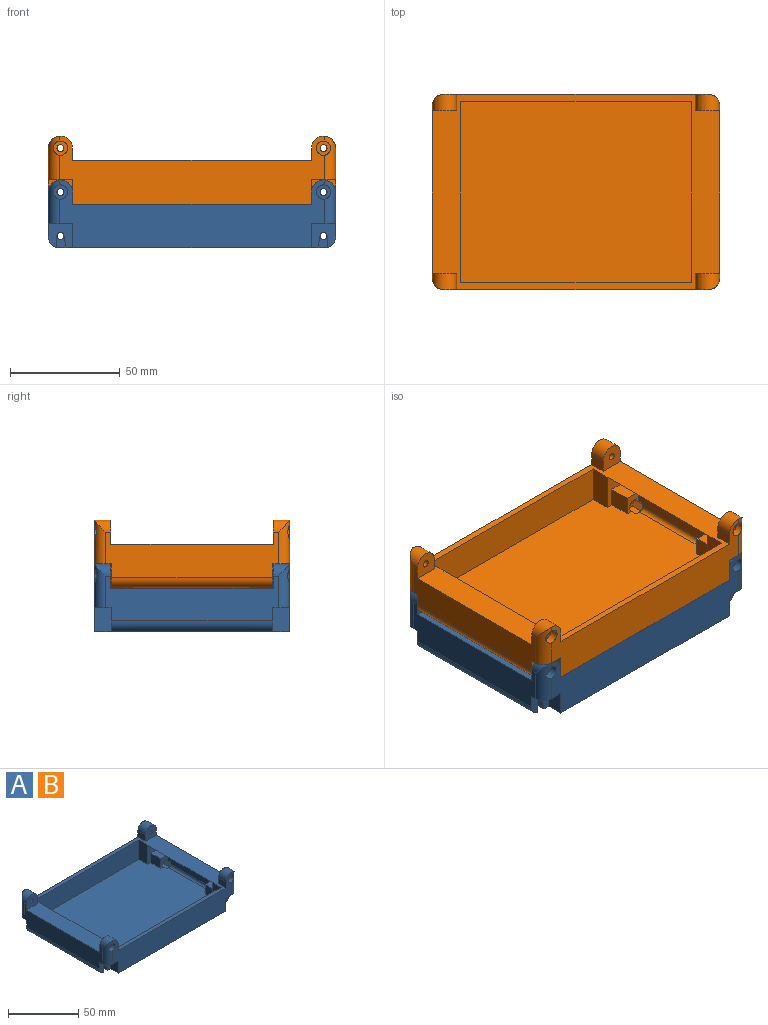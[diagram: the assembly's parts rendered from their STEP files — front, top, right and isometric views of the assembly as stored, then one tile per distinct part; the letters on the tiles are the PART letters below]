
ASSEMBLY  parts=2 mates=1
PART A: 125 faces, bbox 131x89x31 mm
  f0: cylinder r=1.6mm len=11.3mm, axis (0,-1,0), area 60.7mm2, adj f2,f120,f122,f123,f124
  f1: cylinder r=5mm len=73.6mm, axis (0,1,0), area 555.9mm2, adj f2,f8,f32,f33,f108,f110,f122,f124
  f2: plane 11.2x11mm, normal (0,-1,0), area 93.6mm2, adj f0,f1,f32,f33,f45,f46,f122,f123
  f3: plane 121x83mm, normal (0,0,1), area 9527.3mm2, adj f5,f19,f28,f29,f30,f31,f34,f35
  f4: plane 45x6.54mm, normal (-1,0,0), area 283.4mm2, adj f5,f34,f60,f64,f100,f107,f114,f121
  f5: plane 8.54x7mm, normal (0,1,0), area 34mm2, adj f3,f4,f58,f59,f114,f117,f118,f119
  f6: plane 121x31mm, normal (0,-1,0), area 2363mm2, adj f7,f14,f25,f26,f33,f40,f45,f46
  f7: cylinder r=5mm len=19.98mm, axis (0,0,-1), area 126.6mm2, adj f6,f32,f46,f65,f113
  f8: plane 11.2x11mm, normal (0,1,0), area 93.6mm2, adj f1,f9,f32,f33,f47,f48,f108,f109
  f9: cylinder r=1.6mm len=11.3mm, axis (0,1,0), area 60.7mm2, adj f8,f106,f108,f109,f110
  f10: plane 121x31mm, normal (0,1,0), area 2363mm2, adj f11,f20,f33,f36,f39,f40,f47,f48
  f11: cylinder r=5mm len=19.98mm, axis (0,0,-1), area 126.6mm2, adj f10,f32,f48,f68,f99
  f12: plane 11.2x11mm, normal (0,-1,0), area 93.6mm2, adj f13,f16,f27,f33,f49,f50,f94,f95
  f13: cylinder r=1.6mm len=11.3mm, axis (0,-1,0), area 60.7mm2, adj f12,f93,f94,f95,f96
  f14: cylinder r=5mm len=19.98mm, axis (0,0,-1), area 126.6mm2, adj f6,f27,f50,f67,f85
  f15: cylinder r=1.6mm len=11.3mm, axis (0,1,0), area 60.7mm2, adj f17,f79,f80,f81,f82
  f16: cylinder r=5mm len=73.6mm, axis (0,-1,0), area 555.9mm2, adj f12,f17,f27,f33,f80,f82,f94,f96
  f17: plane 11.2x11mm, normal (0,1,0), area 93.6mm2, adj f15,f16,f27,f33,f51,f52,f80,f81
  f18: plane 45x6.54mm, normal (1,0,0), area 283.4mm2, adj f19,f38,f53,f63,f72,f73,f86,f87
  f19: plane 8.54x7mm, normal (0,-1,0), area 34mm2, adj f3,f18,f56,f57,f73,f76,f77,f78
  f20: cylinder r=5mm len=19.98mm, axis (0,0,-1), area 126.6mm2, adj f10,f27,f52,f66,f71
  f21: plane 11x11mm, normal (0,1,0), area 100mm2, adj f25,f32,f40,f65,f111
  f22: plane 11x11mm, normal (0,-1,0), area 100mm2, adj f32,f36,f40,f68,f97
  f23: plane 11x11mm, normal (0,1,0), area 100mm2, adj f26,f27,f40,f67,f83
  f24: plane 11x11mm, normal (0,-1,0), area 100mm2, adj f27,f39,f40,f66,f69
  f25: plane 7.5x5.5mm, normal (-1,0,0), area 41.2mm2, adj f6,f21,f40,f65
  f26: plane 7.5x5.5mm, normal (1,0,0), area 41.2mm2, adj f6,f23,f40,f67
  f27: plane 79x20.5mm, normal (-1,0,0), area 1180.1mm2, adj f12,f14,f16,f17,f20,f23,f24,f40
  f28: plane 17x10mm, normal (0,1,0), area 67.9mm2, adj f3,f44,f58,f59,f64
  f29: plane 17x10mm, normal (0,1,0), area 67.9mm2, adj f3,f42,f54,f55,f63
  f30: plane 17x10mm, normal (0,-1,0), area 67.9mm2, adj f3,f43,f61,f62,f64
  f31: plane 17x10mm, normal (0,-1,0), area 67.9mm2, adj f3,f41,f56,f57,f63
  f32: plane 79x20.5mm, normal (1,0,0), area 1180.1mm2, adj f1,f2,f7,f8,f11,f21,f22,f40
  f33: plane 121x89mm, normal (0,0,-1), area 10456.2mm2, adj f1,f2,f6,f8,f10,f12,f16,f17
  f34: cylinder r=2mm len=39mm, axis (0,1,0), area 122.5mm2, adj f3,f4,f107,f121
  f35: plane 105x17mm, normal (0,1,0), area 1785mm2, adj f3,f40,f42,f44
  f36: plane 7.5x5.5mm, normal (-1,0,0), area 41.2mm2, adj f10,f22,f40,f68
  f37: plane 105x17mm, normal (0,-1,0), area 1785mm2, adj f3,f40,f41,f43
  f38: cylinder r=2mm len=39mm, axis (0,-1,0), area 122.5mm2, adj f3,f18,f72,f86
  f39: plane 7.5x5.5mm, normal (1,0,0), area 41.2mm2, adj f10,f24,f40,f66
  f40: plane 131x89mm, normal (0,0,1), area 2614mm2, adj f6,f10,f21,f22,f23,f24,f25,f26
  f41: plane 17x9mm, normal (1,0,0), area 153mm2, adj f3,f31,f37,f40
  f42: plane 17x9mm, normal (1,0,0), area 153mm2, adj f3,f29,f35,f40
  f43: plane 17x9mm, normal (-1,0,0), area 153mm2, adj f3,f30,f37,f40
  f44: plane 17x9mm, normal (-1,0,0), area 153mm2, adj f3,f28,f35,f40
  f45: plane 11x7.7mm, normal (1,0,0), area 84.7mm2, adj f2,f6,f33,f46
  f46: plane 11.2x7.7mm, normal (0,0,-1), area 80.9mm2, adj f2,f6,f7,f32,f45
  f47: plane 11x7.7mm, normal (1,0,0), area 84.7mm2, adj f8,f10,f33,f48
  f48: plane 11.2x7.7mm, normal (0,0,-1), area 80.9mm2, adj f8,f10,f11,f32,f47
  f49: plane 11x7.7mm, normal (-1,0,0), area 84.7mm2, adj f6,f12,f33,f50
  f50: plane 11.2x7.7mm, normal (0,0,-1), area 80.9mm2, adj f6,f12,f14,f27,f49
  f51: plane 11x7.7mm, normal (-1,0,0), area 84.7mm2, adj f10,f17,f33,f52
  f52: plane 11.2x7.7mm, normal (0,0,-1), area 80.9mm2, adj f10,f17,f20,f27,f51
  f53: plane 8.54x7mm, normal (0,1,0), area 34mm2, adj f3,f18,f54,f55,f87,f88,f89,f90
  f54: plane 10x7mm, normal (0,0,1), area 70mm2, adj f29,f53,f55,f63
  f55: plane 10x8.54mm, normal (1,0,0), area 85.4mm2, adj f3,f29,f53,f54
  f56: plane 10x8.54mm, normal (1,0,0), area 85.4mm2, adj f3,f19,f31,f57
  f57: plane 10x7mm, normal (0,0,1), area 70mm2, adj f19,f31,f56,f63
  f58: plane 10x8.54mm, normal (-1,0,0), area 85.4mm2, adj f3,f5,f28,f59
  f59: plane 10x7mm, normal (0,0,1), area 70mm2, adj f5,f28,f58,f64
  f60: plane 8.54x7mm, normal (0,-1,0), area 34mm2, adj f3,f4,f61,f62,f100,f101,f102,f103
  f61: plane 10x7mm, normal (0,0,1), area 70mm2, adj f30,f60,f62,f64
  f62: plane 10x8.54mm, normal (-1,0,0), area 85.4mm2, adj f3,f30,f60,f61
  f63: plane 65x10mm, normal (0.65,0,-0.76), area 851.5mm2, adj f18,f29,f31,f40,f54,f57
  f64: plane 65x10mm, normal (-0.65,0,-0.76), area 851.5mm2, adj f4,f28,f30,f40,f59,f61
  f65: cylinder r=5.5mm len=11mm, axis (0,1,0), area 114.7mm2, adj f6,f7,f21,f25,f32
  f66: cylinder r=5.5mm len=11mm, axis (0,1,0), area 114.7mm2, adj f10,f20,f24,f27,f39
  f67: cylinder r=5.5mm len=11mm, axis (0,1,0), area 114.7mm2, adj f6,f14,f23,f26,f27
  f68: cylinder r=5.5mm len=11mm, axis (0,1,0), area 114.7mm2, adj f10,f11,f22,f32,f36
  f69: cylinder r=1.6mm len=3.68mm, axis (0,1,0), area 37mm2, adj f24,f70
  f70: plane 6.5x6.5mm, normal (0,1,0), area 25.1mm2, adj f69,f71
  f71: cylinder r=3.25mm len=6.5mm, axis (0,1,0), area 74.3mm2, adj f10,f20,f70
  f72: plane 5.06x4.11mm, normal (0,1,0), area 2.5mm2, adj f3,f18,f38,f73,f74,f75,f76
  f73: plane 6x2.81mm, normal (0.87,0,-0.5), area 14.3mm2, adj f18,f19,f72,f74,f78,f79
  f74: plane 6x2.81mm, normal (0.87,0,0.5), area 19.5mm2, adj f72,f73,f75,f79
  f75: plane 6x3.25mm, normal (0,0,1), area 19.5mm2, adj f72,f74,f76,f79
  f76: plane 6x2.81mm, normal (-0.87,0,0.5), area 10.8mm2, adj f3,f19,f72,f75,f77,f79
  f77: plane 3x2.81mm, normal (-0.87,0,-0.5), area 9.8mm2, adj f19,f76,f78,f79
  f78: plane 3.25x3mm, normal (0,0,-1), area 9.7mm2, adj f19,f73,f77,f79
  f79: plane 6.5x5.63mm, normal (0,-1,0), area 19.4mm2, adj f15,f73,f74,f75,f76,f77,f78
  f80: plane 10x5.38mm, normal (1,0,0), area 53.8mm2, adj f15,f16,f17,f82
  f81: plane 10x5.77mm, normal (-0.99,0,-0.17), area 58.5mm2, adj f15,f17,f33,f82
  f82: plane 5.76x4.15mm, normal (0,1,0), area 16.2mm2, adj f15,f16,f33,f80,f81
  f83: cylinder r=1.6mm len=3.68mm, axis (0,-1,0), area 37mm2, adj f23,f84
  f84: plane 6.5x6.5mm, normal (0,-1,0), area 25.1mm2, adj f83,f85
  f85: cylinder r=3.25mm len=6.5mm, axis (0,-1,0), area 74.3mm2, adj f6,f14,f84
  f86: plane 5.06x4.11mm, normal (0,-1,0), area 2.5mm2, adj f3,f18,f38,f87,f90,f91,f92
  f87: plane 6x2.81mm, normal (0.87,0,-0.5), area 14.3mm2, adj f18,f53,f86,f88,f92,f93
  f88: plane 3.25x3mm, normal (0,0,-1), area 9.7mm2, adj f53,f87,f89,f93
  f89: plane 3x2.81mm, normal (-0.87,0,-0.5), area 9.8mm2, adj f53,f88,f90,f93
  f90: plane 6x2.81mm, normal (-0.87,0,0.5), area 10.8mm2, adj f3,f53,f86,f89,f91,f93
  f91: plane 6x3.25mm, normal (0,0,1), area 19.5mm2, adj f86,f90,f92,f93
  f92: plane 6x2.81mm, normal (0.87,0,0.5), area 19.5mm2, adj f86,f87,f91,f93
  f93: plane 6.5x5.63mm, normal (0,1,0), area 19.4mm2, adj f13,f87,f88,f89,f90,f91,f92
  f94: plane 10x5.38mm, normal (1,0,0), area 53.8mm2, adj f12,f13,f16,f96
  f95: plane 10x5.77mm, normal (-0.99,0,-0.17), area 58.5mm2, adj f12,f13,f33,f96
  f96: plane 5.76x4.15mm, normal (0,-1,0), area 16.2mm2, adj f13,f16,f33,f94,f95
  f97: cylinder r=1.6mm len=3.68mm, axis (0,1,0), area 37mm2, adj f22,f98
  f98: plane 6.5x6.5mm, normal (0,1,0), area 25.1mm2, adj f97,f99
  f99: cylinder r=3.25mm len=6.5mm, axis (0,1,0), area 74.3mm2, adj f10,f11,f98
  f100: plane 6x2.81mm, normal (-0.87,0,-0.5), area 14.3mm2, adj f4,f60,f101,f105,f106,f107
  f101: plane 3.25x3mm, normal (0,0,-1), area 9.7mm2, adj f60,f100,f102,f106
  f102: plane 3x2.81mm, normal (0.87,0,-0.5), area 9.8mm2, adj f60,f101,f103,f106
  f103: plane 6x2.81mm, normal (0.87,0,0.5), area 10.8mm2, adj f3,f60,f102,f104,f106,f107
  f104: plane 6x3.25mm, normal (0,0,1), area 19.5mm2, adj f103,f105,f106,f107
  f105: plane 6x2.81mm, normal (-0.87,0,0.5), area 19.5mm2, adj f100,f104,f106,f107
  f106: plane 6.5x5.63mm, normal (0,-1,0), area 19.4mm2, adj f9,f100,f101,f102,f103,f104,f105
  f107: plane 5.06x4.11mm, normal (0,1,0), area 2.5mm2, adj f3,f4,f34,f100,f103,f104,f105
  f108: plane 10x5.38mm, normal (-1,0,0), area 53.8mm2, adj f1,f8,f9,f110
  f109: plane 10x5.77mm, normal (0.99,0,-0.17), area 58.5mm2, adj f8,f9,f33,f110
  f110: plane 5.76x4.15mm, normal (0,1,0), area 16.2mm2, adj f1,f9,f33,f108,f109
  f111: cylinder r=1.6mm len=3.68mm, axis (0,-1,0), area 37mm2, adj f21,f112
  f112: plane 6.5x6.5mm, normal (0,-1,0), area 25.1mm2, adj f111,f113
  f113: cylinder r=3.25mm len=6.5mm, axis (0,-1,0), area 74.3mm2, adj f6,f7,f112
  f114: plane 6x2.81mm, normal (-0.87,0,-0.5), area 14.3mm2, adj f4,f5,f115,f119,f120,f121
  f115: plane 6x2.81mm, normal (-0.87,0,0.5), area 19.5mm2, adj f114,f116,f120,f121
  f116: plane 6x3.25mm, normal (0,0,1), area 19.5mm2, adj f115,f117,f120,f121
  f117: plane 6x2.81mm, normal (0.87,0,0.5), area 10.8mm2, adj f3,f5,f116,f118,f120,f121
  f118: plane 3x2.81mm, normal (0.87,0,-0.5), area 9.8mm2, adj f5,f117,f119,f120
  f119: plane 3.25x3mm, normal (0,0,-1), area 9.7mm2, adj f5,f114,f118,f120
  f120: plane 6.5x5.63mm, normal (0,1,0), area 19.4mm2, adj f0,f114,f115,f116,f117,f118,f119
  f121: plane 5.06x4.11mm, normal (0,-1,0), area 2.5mm2, adj f3,f4,f34,f114,f115,f116,f117
  f122: plane 10x5.38mm, normal (-1,0,0), area 53.8mm2, adj f0,f1,f2,f124
  f123: plane 10x5.77mm, normal (0.99,0,-0.17), area 58.5mm2, adj f0,f2,f33,f124
  f124: plane 5.76x4.15mm, normal (0,-1,0), area 16.2mm2, adj f0,f1,f33,f122,f123
PART B: same geometry as A
PLACE A t=(-7.7,9.82,-12.14)mm
PLACE B t=(-7.7,9.77,7.86)mm
MATE fastened B.f15 <-> A.f66  axis (0,1,0) through (-57.7,40.07,13.36)mm
